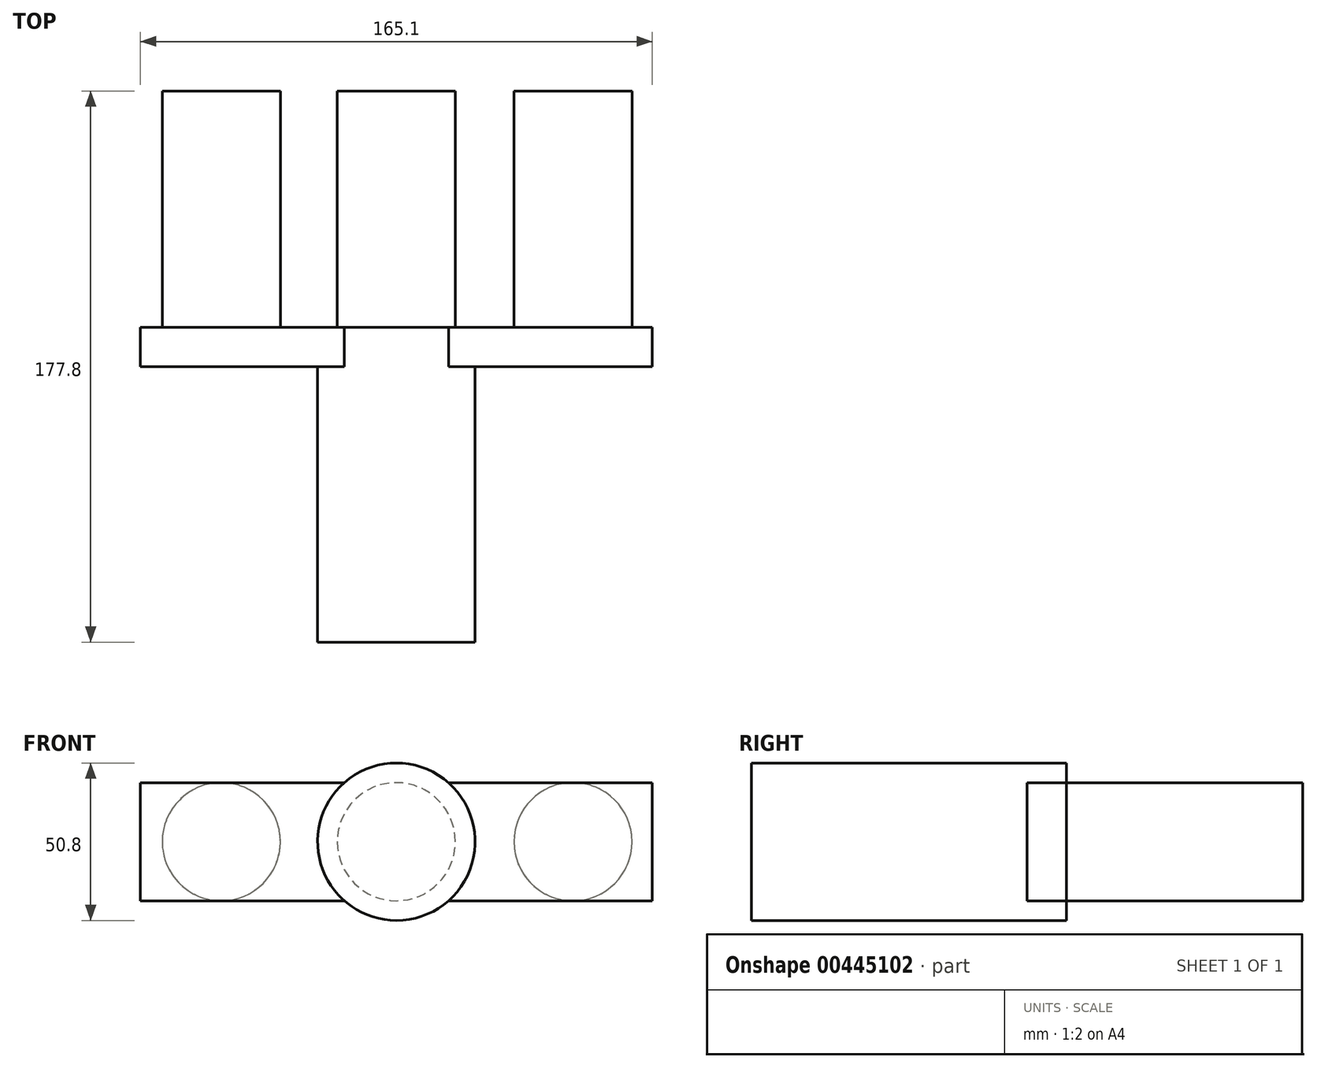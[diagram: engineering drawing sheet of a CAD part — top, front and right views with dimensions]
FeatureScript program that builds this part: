
annotation { "Feature Type Name" : "Feature", "Feature Type Description" : "" }
export const myFeature = defineFeature(function(context is Context, id is Id, definition is map)
    precondition{}
    {
        {
            var Q0;
            Q0=qCreatedBy(makeId("Front.planeOp"),FACE);
            var sketch = newSketch(context, id + "F0", { "sketchPlane" : qUnion([Q0])});
            skLineSegment(sketch, "E0.bottom", {"start": v(82.55, 19.05) * mm, "end": v(-82.55, 19.05) * mm});
            skLineSegment(sketch, "E0.top", {"start": v(82.55, -19.05) * mm, "end": v(-82.55, -19.05) * mm});
            skLineSegment(sketch, "E0.left", {"start": v(82.55, 19.05) * mm, "end": v(82.55, -19.05) * mm});
            skLineSegment(sketch, "E0.right", {"start": v(-82.55, 19.05) * mm, "end": v(-82.55, -19.05) * mm});
            skPoint(sketch, "E0.middle", {"position": v(0, 0) * mm});
            skSolve(sketch);
        }
        {
            var Q0;
            Q0 = qSketchRegion(id + "F0", true);
            extrude(context, id + "F1", {"entities" : qUnion([Q0]), "depth" : 12.7 * mm});
        }
        {
            var Q0;
            Q0=qCreatedBy(makeId("Front.planeOp"),FACE);
            var sketch = newSketch(context, id + "F2", { "sketchPlane" : qUnion([Q0])});
            skCircle(sketch, "E1", {"center": v(0, 0) * mm, "radius": 25.4 * mm});
            skSolve(sketch);
        }
        {
            var Q0;
            Q0 = qSketchRegion(id + "F2", true);
            extrude(context, id + "F3", {"entities" : qUnion([Q0]), "operationType" : NewBodyOperationType.ADD, "depth" : 101.6 * mm});
        }
        {
            var Q0;
            Q0=qCreatedBy(makeId("Front.planeOp"),FACE);
            var sketch = newSketch(context, id + "F4", { "sketchPlane" : qUnion([Q0])});
            skCircle(sketch, "E2", {"center": v(56.97, 0) * mm, "radius": 19.05 * mm});
            skCircle(sketch, "E3", {"center": v(-56.47, 0) * mm, "radius": 19.05 * mm});
            skCircle(sketch, "E4", {"center": v(0, 0) * mm, "radius": 19.05 * mm});
            skSolve(sketch);
        }
        {
            var Q0;
            Q0 = qSketchRegion(id + "F4", true);
            extrude(context, id + "F5", {"entities" : qUnion([Q0]), "operationType" : NewBodyOperationType.ADD, "oppositeDirection" : true, "depth" : 76.2 * mm});
        }
    });
